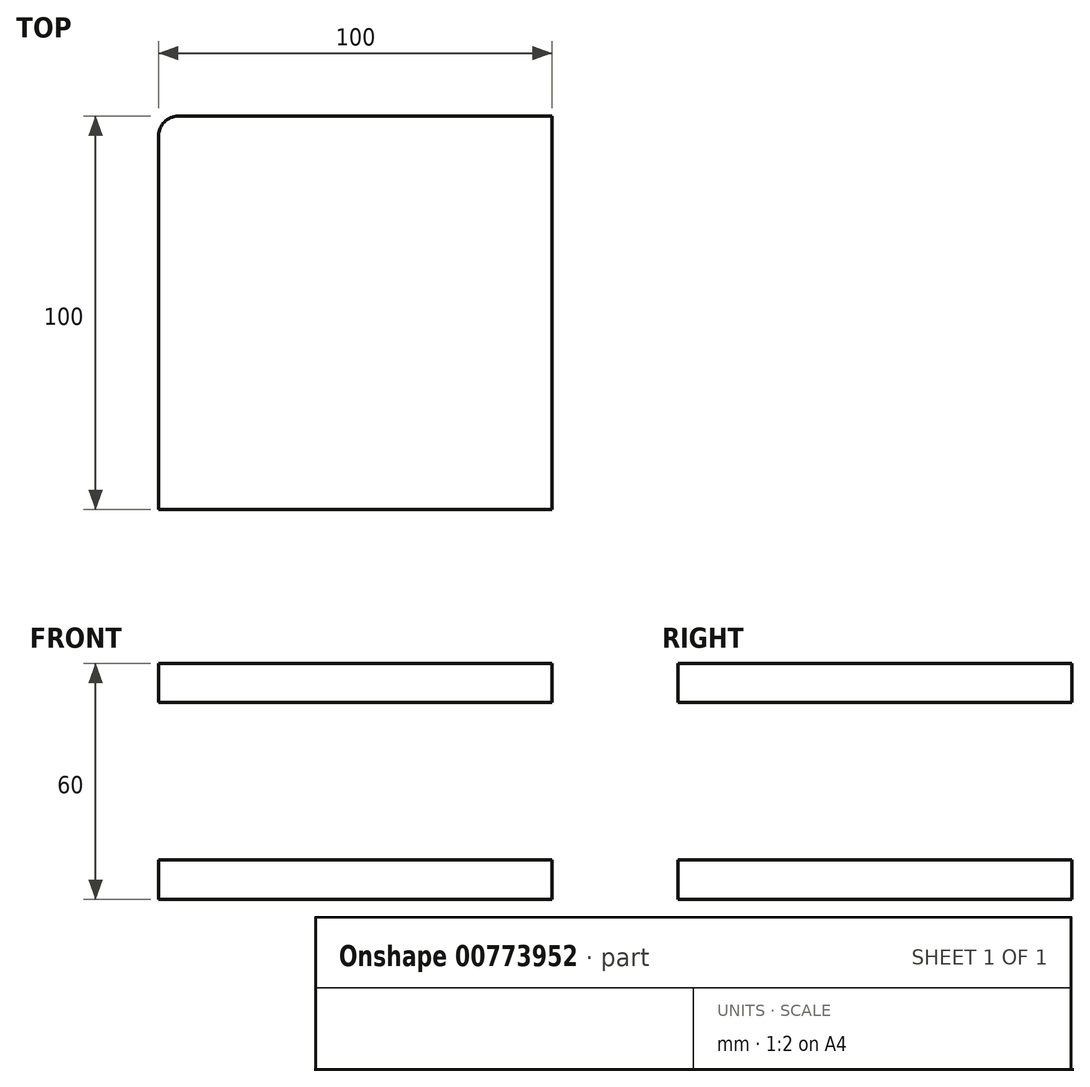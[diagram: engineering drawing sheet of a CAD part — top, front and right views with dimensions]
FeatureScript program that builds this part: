
annotation { "Feature Type Name" : "Feature", "Feature Type Description" : "" }
export const myFeature = defineFeature(function(context is Context, id is Id, definition is map)
    precondition{}
    {
        {
            var Q0;
            Q0=qCreatedBy(makeId("Top.planeOp"),FACE);
            var sketch = newSketch(context, id + "F0", { "sketchPlane" : qUnion([Q0])});
            skLineSegment(sketch, "E0.bottom", {"start": v(-50, 50) * mm, "end": v(50, 50) * mm});
            skLineSegment(sketch, "E0.top", {"start": v(-50, -50) * mm, "end": v(50, -50) * mm});
            skLineSegment(sketch, "E0.left", {"start": v(-50, 50) * mm, "end": v(-50, -50) * mm});
            skLineSegment(sketch, "E0.right", {"start": v(50, 50) * mm, "end": v(50, -50) * mm});
            skPoint(sketch, "E0.middle", {"position": v(0, 0) * mm});
            skSolve(sketch);
        }
        {
            var Q0;
            Q0=qSketchRegion(id+"F0",true);
            extrude(context, id + "F1", {"entities" : qUnion([Q0]), "depth" : 60 * mm, "offsetDistance" : 25 * mm});
        }
        {
            var Q0;
            Q0=qCreatedBy(makeId("Top.planeOp"),FACE);
            var sketch = newSketch(context, id + "F2", { "sketchPlane" : qUnion([Q0])});
            skLineSegment(sketch, "E1.bottom", {"start": v(-60, 60) * mm, "end": v(60, 60) * mm});
            skLineSegment(sketch, "E1.top", {"start": v(-60, -60) * mm, "end": v(60, -60) * mm});
            skLineSegment(sketch, "E1.left", {"start": v(-60, 60) * mm, "end": v(-60, -60) * mm});
            skLineSegment(sketch, "E1.right", {"start": v(60, 60) * mm, "end": v(60, -60) * mm});
            skPoint(sketch, "E1.middle", {"position": v(0, 0) * mm});
            skSolve(sketch);
        }
        {
            var Q0;
            Q0=makeQuery(id+"F1.opExtrude","CAP_FACE",FACE,{"disambiguationData":[OSD([sQuery(id+"F0.wireOp",EDGE,"E0.bottom"),sQuery(id+"F0.wireOp",EDGE,"E0.top"),sQuery(id+"F0.wireOp",EDGE,"E0.left"),sQuery(id+"F0.wireOp",EDGE,"E0.right")])],"isStart":false});
            extrude(context, id + "F3", {"entities" : qUnion([Q0]), "operationType" : NewBodyOperationType.REMOVE, "oppositeDirection" : true, "depth" : 50 * mm, "offsetDistance" : 25 * mm, "hasSecondDirection" : true, "secondDirectionOppositeDirection" : true, "secondDirectionDepth" : 10 * mm});
        }
        {
            var Q0;
            Q0=makeQuery(id+"F1.opExtrude","SWEPT_EDGE",EDGE,{"disambiguationData":[OSD([sQuery(id+"F0.wireOp",EDGE,"E0.bottom"),sQuery(id+"F0.wireOp",EDGE,"E0.left")])]});
            var Q1;
            Q1=makeQuery(id+"F3.boolean.opBoolean","COPY",EDGE,{"derivedFrom":makeQuery(id+"F3.opExtrude","SWEPT_EDGE",EDGE,{"disambiguationData":[OSD([sQuery(id+"F2.wireOp",EDGE,"E1.bottom"),sQuery(id+"F2.wireOp",EDGE,"E1.right")])]})});
            var Q2;
            Q2=makeQuery(id+"F3.boolean.opBoolean","COPY",EDGE,{"derivedFrom":makeQuery(id+"F3.opExtrude","SWEPT_EDGE",EDGE,{"disambiguationData":[OSD([sQuery(id+"F2.wireOp",EDGE,"E1.top"),sQuery(id+"F2.wireOp",EDGE,"E1.left")])]})});
            var Q3;
            Q3=makeQuery(id+"F3.boolean.opBoolean","COPY",EDGE,{"derivedFrom":makeQuery(id+"F3.opExtrude","SWEPT_EDGE",EDGE,{"disambiguationData":[OSD([sQuery(id+"F2.wireOp",EDGE,"E1.top"),sQuery(id+"F2.wireOp",EDGE,"E1.right")])]})});
            fillet(context, id + "F4", {"entities" : qUnion([Q0, Q1, Q2, Q3]), "radius" : 5 * mm, "tangentPropagation" : true, "allowEdgeOverflow" : false});
        }
    });
